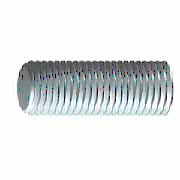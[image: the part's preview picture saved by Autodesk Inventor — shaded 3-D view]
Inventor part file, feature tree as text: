
AUTODESK INVENTOR PART (.ipt)
format: ipt  version: 2015 (Build 190159000, 159)  size: 117,760 bytes
history: native  units: mm
features: revolve x1, sketch x1
ambient origin geometry x8: Origin, YZ Plane, XZ Plane, XY Plane, X Axis, Y Axis, Z Axis, Center Point
bodies: Solid1 (feature_tree)
feature tree (2):
  revolve  "Revolution 1"  [1 undecoded]
  sketch  "Sketch 1"  dims[d2=90.0deg d3=10.0mm d4=0.0mm d5=0.0mm d6=0.0mm d7=0.0mm]
note: 1 required parameter value undecoded (feature->parameter linkage not recoverable at this tier; creation-order binding heuristic only, values carry confidence <= 0.55)
